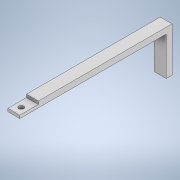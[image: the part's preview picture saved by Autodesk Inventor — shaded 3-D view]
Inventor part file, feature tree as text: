
AUTODESK INVENTOR PART (.ipt)
format: ipt  version: 2020.2 (Build 242310000, 310)  size: 124,416 bytes
history: native  units: mm
features: extrude x3, sketch x3
ambient origin geometry x8: Origin, YZ Plane, XZ Plane, XY Plane, X Axis, Y Axis, Z Axis, Center Point
bodies: Solid1 (feature_tree)
feature tree (6):
  extrude  "Extrusion1"  Depth=98.806mm
  extrude  "Extrusion2"  Depth=8.0mm
  extrude  "Extrusion3"  Depth=30.0mm
  sketch  "Sketch1"  dims[d0=8.0mm d1=98.806mm]
  sketch  "Sketch2"  dims[d2=90.0deg d3=8.0mm]
  sketch  "Sketch3"  dims[d4=98.806mm d5=5.0mm d6=3.4mm d7=4.0mm d8=0.0mm d9=8.0mm d10=2.0mm d11=12.54mm d12=0.0mm d13=8.0mm d14=4.0mm d15=30.0mm d16=0.0mm]
